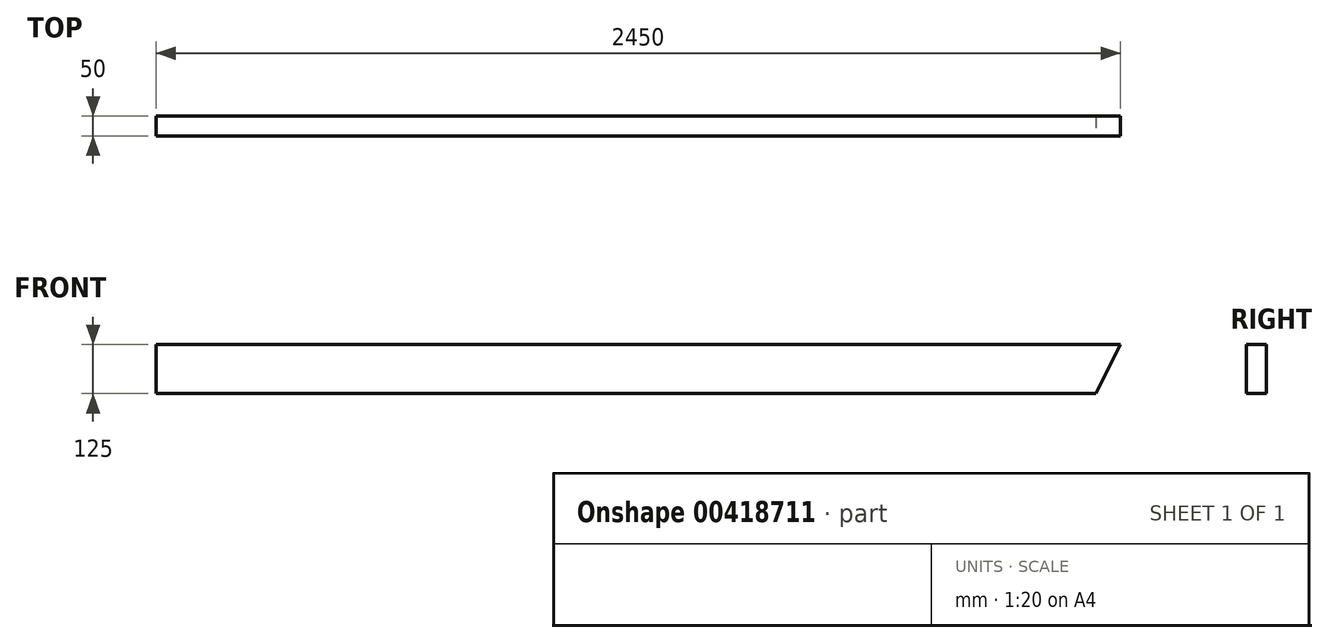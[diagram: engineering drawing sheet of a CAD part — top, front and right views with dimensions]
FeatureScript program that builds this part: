
annotation { "Feature Type Name" : "Feature", "Feature Type Description" : "" }
export const myFeature = defineFeature(function(context is Context, id is Id, definition is map)
    precondition{}
    {
        {
            var Q0;
            Q0=qCreatedBy(makeId("Right.planeOp"),FACE);
            var sketch = newSketch(context, id + "F0", { "sketchPlane" : qUnion([Q0])});
            skLineSegment(sketch, "E0.bottom", {"start": v(25, 62.5) * mm, "end": v(-25, 62.5) * mm});
            skLineSegment(sketch, "E0.top", {"start": v(25, -62.5) * mm, "end": v(-25, -62.5) * mm});
            skLineSegment(sketch, "E0.left", {"start": v(25, 62.5) * mm, "end": v(25, -62.5) * mm});
            skLineSegment(sketch, "E0.right", {"start": v(-25, 62.5) * mm, "end": v(-25, -62.5) * mm});
            skPoint(sketch, "E0.middle", {"position": v(0, 0) * mm});
            skSolve(sketch);
        }
        {
            var Q0;
            Q0=qSketchRegion(id+"F0",true);
            extrude(context, id + "F1", {"entities" : qUnion([Q0]), "oppositeDirection" : true, "depth" : 2450 * mm});
        }
        {
            var Q0;
            Q0=qCreatedBy(makeId("Front.planeOp"),FACE);
            var sketch = newSketch(context, id + "F2", { "sketchPlane" : qUnion([Q0])});
            skLineSegment(sketch, "E1", {"start": v(0, 62.5) * mm, "end": v(0, -62.5) * mm});
            skLineSegment(sketch, "E2", {"start": v(0, -62.5) * mm, "end": v(-62.5, -62.5) * mm});
            skLineSegment(sketch, "E3", {"start": v(-62.5, -62.5) * mm, "end": v(0, 62.5) * mm});
            skSolve(sketch);
        }
        {
            var Q0;
            Q0=qSketchRegion(id+"F2",true);
            extrude(context, id + "F3", {"entities" : qUnion([Q0]), "operationType" : NewBodyOperationType.REMOVE, "endBound" : BoundingType.UP_TO_NEXT, "oppositeDirection" : true, "depth" : 25 * mm, "hasSecondDirection" : true, "secondDirectionBound" : SecondDirectionBoundingType.UP_TO_NEXT, "secondDirectionOppositeDirection" : false, "secondDirectionDepth" : 25 * mm});
        }
    });
